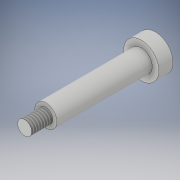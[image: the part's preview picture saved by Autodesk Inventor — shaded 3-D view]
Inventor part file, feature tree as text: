
AUTODESK INVENTOR PART (.ipt)
format: ipt  version: 2019 (Build 230136000, 136)  size: 110,592 bytes
history: native  units: in
note: dims shown in document units (in); Inventor stores cm internally (conversion verified against a paired STEP export)
features: revolve x1, thread x1, sketch x1
ambient origin geometry x8: Origin, YZ Plane, XZ Plane, XY Plane, X Axis, Y Axis, Z Axis, Center Point
bodies: Solid1 (feature_tree)
feature tree (3):
  revolve  "Revolution1"  [1 undecoded]
  thread  "Thread1"  [1 undecoded]
  sketch  "Sketch1"  dims[d0=3.7in d1=0.4in d2=2.7in d3=0.2in d4=0.3125in d5=0.5in d6=90.0deg d7=1.0in d8=0.0in]
note: 2 required parameter values undecoded (feature->parameter linkage not recoverable at this tier; creation-order binding heuristic only, values carry confidence <= 0.55)